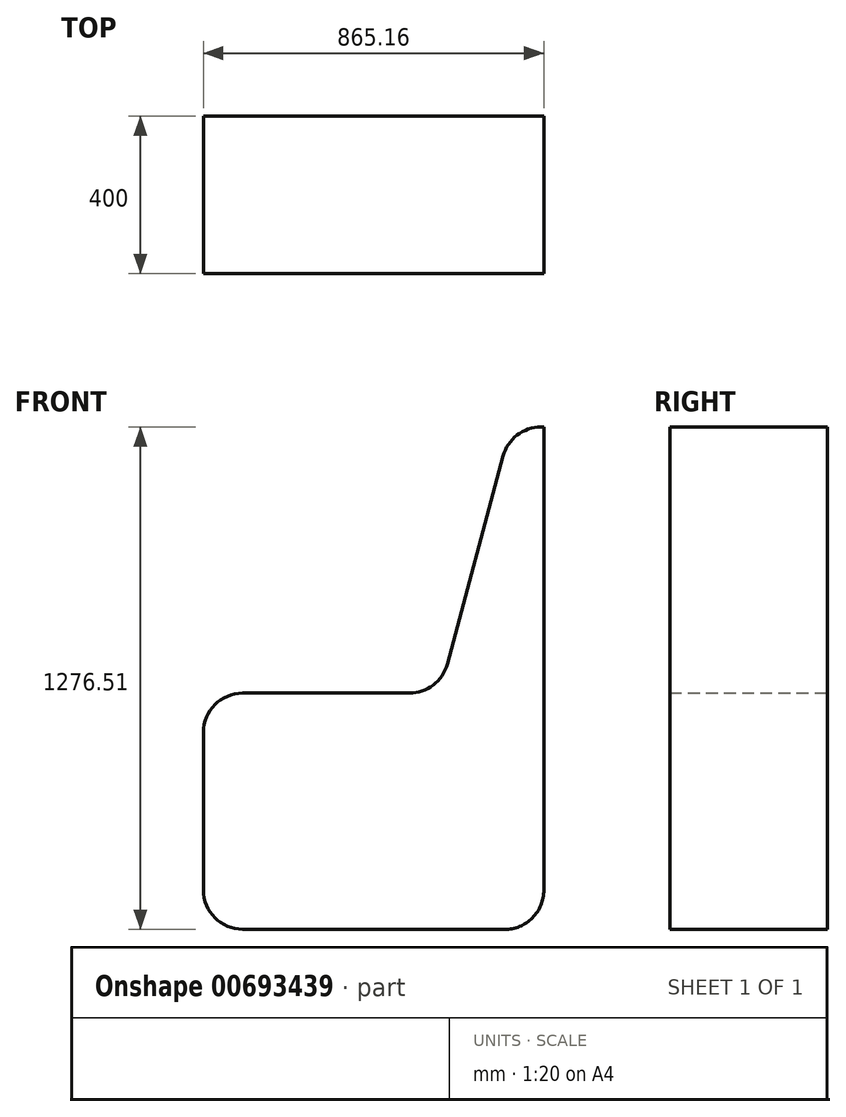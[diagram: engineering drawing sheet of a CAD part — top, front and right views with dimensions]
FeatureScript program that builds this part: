
annotation { "Feature Type Name" : "Feature", "Feature Type Description" : "" }
export const myFeature = defineFeature(function(context is Context, id is Id, definition is map)
    precondition{}
    {
        {
            var Q0;
            Q0=qCreatedBy(makeId("Front.planeOp"),FACE);
            cPlane(context, id + "F0", {"entities" : qUnion([Q0]), "cplaneType" : CPlaneType.OFFSET, "offset" : 500 * mm, "width" : 150 * mm, "height" : 150 * mm});
        }
        {
            var Q0;
            Q0=qCreatedBy(id+"F0.planeOp",FACE);
            var sketch = newSketch(context, id + "F1", { "sketchPlane" : qUnion([Q0])});
            skLineSegment(sketch, "E0", {"start": v(-781.17, -402.11) * mm, "end": v(-781.17, 197.89) * mm});
            skLineSegment(sketch, "E1", {"start": v(-781.17, 197.89) * mm, "end": v(-181.17, 197.89) * mm});
            skLineSegment(sketch, "E2", {"start": v(-181.17, 197.89) * mm, "end": v(0, 874.03) * mm});
            skLineSegment(sketch, "E3", {"start": v(0, 874.03) * mm, "end": v(83.99, 874.03) * mm});
            skLineSegment(sketch, "E4", {"start": v(83.99, 874.03) * mm, "end": v(83.99, -402.53) * mm});
            skLineSegment(sketch, "E5", {"start": v(83.99, -402.53) * mm, "end": v(-781.17, -402.11) * mm});
            skSolve(sketch);
        }
        {
            var Q0;
            Q0=makeQuery(id+"F1.imprint","IMPRINT",FACE,{"disambiguationData":[TD([[makeQuery(id+"F1.imprint","IMPRINT",EDGE,{"derivedFrom":sQuery(id+"F1.wireOp",EDGE,"E0")}),-1.0]])]});
            extrude(context, id + "F2", {"entities" : qUnion([Q0]), "depth" : 400 * mm, "offsetDistance" : 25 * mm});
        }
        {
            var Q0;
            Q0=makeQuery(id+"F2.opExtrude","SWEPT_EDGE",EDGE,{"disambiguationData":[OSD([sQuery(id+"F1.wireOp",EDGE,"E0"),sQuery(id+"F1.wireOp",EDGE,"E1")])]});
            var Q1;
            Q1=makeQuery(id+"F2.opExtrude","SWEPT_EDGE",EDGE,{"disambiguationData":[OSD([sQuery(id+"F1.wireOp",EDGE,"E2"),sQuery(id+"F1.wireOp",EDGE,"E3")])]});
            var Q2;
            Q2=makeQuery(id+"F2.opExtrude","SWEPT_EDGE",EDGE,{"disambiguationData":[OSD([sQuery(id+"F1.wireOp",EDGE,"E1"),sQuery(id+"F1.wireOp",EDGE,"E2")])]});
            var Q3;
            Q3=makeQuery(id+"F2.opExtrude","SWEPT_EDGE",EDGE,{"disambiguationData":[OSD([sQuery(id+"F1.wireOp",EDGE,"E0"),sQuery(id+"F1.wireOp",EDGE,"E5")])]});
            var Q4;
            Q4=makeQuery(id+"F2.opExtrude","SWEPT_EDGE",EDGE,{"disambiguationData":[OSD([sQuery(id+"F1.wireOp",EDGE,"E4"),sQuery(id+"F1.wireOp",EDGE,"E5")])]});
            fillet(context, id + "F3", {"entities" : qUnion([Q0, Q1, Q2, Q3, Q4]), "radius" : 100 * mm, "tangentPropagation" : true, "allowEdgeOverflow" : false});
        }
        {
            var Q0;
            Q0=makeQuery(id+"F2.opExtrude","CAP_FACE",FACE,{"disambiguationData":[OSD([sQuery(id+"F1.wireOp",EDGE,"E0"),sQuery(id+"F1.wireOp",EDGE,"E1"),sQuery(id+"F1.wireOp",EDGE,"E2"),sQuery(id+"F1.wireOp",EDGE,"E3"),sQuery(id+"F1.wireOp",EDGE,"E4"),sQuery(id+"F1.wireOp",EDGE,"E5")])],"isStart":false});
            var sketch = newSketch(context, id + "F4", { "sketchPlane" : qUnion([Q0])});
            skLineSegment(sketch, "E6.0", {"start": v(-681.17, 197.89) * mm, "end": v(-257.9, 197.89) * mm});
            skArc(sketch, "E6.1", {"start": v(-681.17, 197.89) * mm, "mid": v(-751.88, 168.6) * mm, "end": v(-781.17, 97.89) * mm});
            skArc(sketch, "E6.2", {"start": v(-161.31, 272) * mm, "mid": v(-197.03, 218.55) * mm, "end": v(-257.9, 197.89) * mm});
            skLineSegment(sketch, "E7.0", {"start": v(-161.31, 272) * mm, "end": v(-19.86, 799.92) * mm});
            skArc(sketch, "E8.0", {"start": v(76.73, 874.03) * mm, "mid": v(15.86, 853.37) * mm, "end": v(-19.86, 799.92) * mm});
            skLineSegment(sketch, "E9.0", {"start": v(-781.17, -302.16) * mm, "end": v(-781.17, 97.89) * mm});
            skArc(sketch, "E9.1", {"start": v(-781.17, -302.16) * mm, "mid": v(-751.9, -372.86) * mm, "end": v(-681.22, -402.16) * mm});
            skLineSegment(sketch, "E10.0", {"start": v(-16.06, -402.48) * mm, "end": v(-681.22, -402.16) * mm});
            skSolve(sketch);
        }
        {
            var Q0;
            Q0=sQuery(id+"F4.wireOp",EDGE,"E9.1");
            var Q1;
            Q1=sQuery(id+"F4.wireOp",EDGE,"E8.0");
            var Q2;
            Q2=sQuery(id+"F4.wireOp",EDGE,"E6.2");
            var Q3;
            Q3=sQuery(id+"F4.wireOp",EDGE,"E10.0");
            var Q4;
            Q4=sQuery(id+"F4.wireOp",EDGE,"E6.1");
            extrude(context, id + "F5", {"bodyType" : ToolBodyType.SURFACE, "surfaceEntities" : qUnion([Q0, Q1, Q2, Q3, Q4]), "oppositeDirection" : true, "depth" : 300 * mm, "offsetDistance" : 25 * mm});
        }
        {
            var Q0;
            Q0=makeQuery(id+"F5.opExtrude","SWEPT_BODY",BODY,{"disambiguationData":[OSD([sQuery(id+"F4.wireOp",EDGE,"E6.1")])]});
            var Q1;
            Q1=makeQuery(id+"F5.opExtrude","SWEPT_BODY",BODY,{"disambiguationData":[OSD([sQuery(id+"F4.wireOp",EDGE,"E6.2")])]});
            var Q2;
            Q2=makeQuery(id+"F5.opExtrude","SWEPT_BODY",BODY,{"disambiguationData":[OSD([sQuery(id+"F4.wireOp",EDGE,"E8.0")])]});
            var Q3;
            Q3=makeQuery(id+"F5.opExtrude","SWEPT_BODY",BODY,{"disambiguationData":[OSD([sQuery(id+"F4.wireOp",EDGE,"E10.0")])]});
            var Q4;
            Q4=makeQuery(id+"F4.imprint","IMPRINT",FACE,{"disambiguationData":[TD([[makeQuery(id+"F4.imprint","IMPRINT",EDGE,{"derivedFrom":sQuery(id+"F4.wireOp",EDGE,"E6.0")}),-1.0]])]});
            mirror(context, id + "F6", {"entities" : qUnion([Q0, Q1, Q2, Q3]), "mirrorPlane" : qUnion([Q4])});
        }
    });
